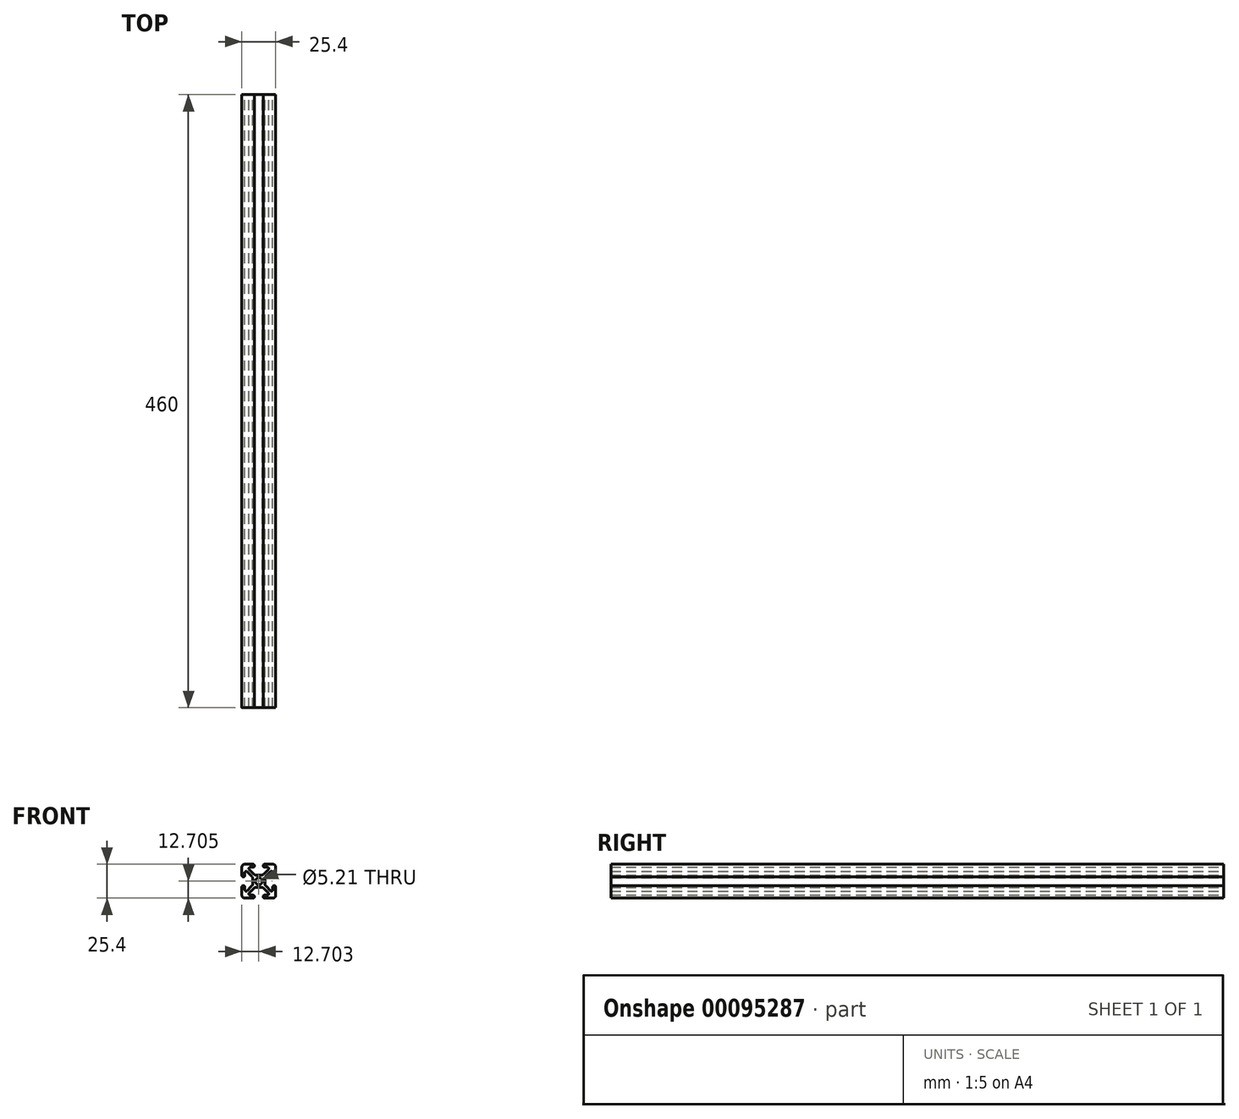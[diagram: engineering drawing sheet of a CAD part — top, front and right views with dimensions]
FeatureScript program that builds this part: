
annotation { "Feature Type Name" : "Feature", "Feature Type Description" : "" }
export const myFeature = defineFeature(function(context is Context, id is Id, definition is map)
    precondition{}
    {
        {
            var Q0;
            Q0=qCreatedBy(makeId("Front.planeOp"),FACE);
            var sketch = newSketch(context, id + "F0", { "sketchPlane" : qUnion([Q0])});
            skArc(sketch, "E0", {"start": v(-10.62, 12.76) * mm, "mid": v(-12.1, 12.15) * mm, "end": v(-12.73, 10.66) * mm});
            skArc(sketch, "E1", {"start": v(-12.73, 4.4) * mm, "mid": v(-11.62, 3.3) * mm, "end": v(-10.52, 4.4) * mm});
            skArc(sketch, "E2", {"start": v(-4.37, 10.55) * mm, "mid": v(-3.27, 11.66) * mm, "end": v(-4.37, 12.76) * mm});
            skArc(sketch, "E3", {"start": v(-8.75, 7.2) * mm, "mid": v(-9.88, 7.42) * mm, "end": v(-10.52, 6.46) * mm});
            skArc(sketch, "E4", {"start": v(-6.43, 10.55) * mm, "mid": v(-7.38, 9.92) * mm, "end": v(-7.16, 8.8) * mm});
            skLineSegment(sketch, "E5", {"start": v(-12.73, 10.66) * mm, "end": v(-12.73, 4.4) * mm});
            skLineSegment(sketch, "E6", {"start": v(-10.62, 12.76) * mm, "end": v(-4.37, 12.76) * mm});
            skLineSegment(sketch, "E7", {"start": v(-10.52, 4.4) * mm, "end": v(-10.52, 6.46) * mm});
            skLineSegment(sketch, "E8", {"start": v(-4.37, 10.55) * mm, "end": v(-6.43, 10.55) * mm});
            skLineSegment(sketch, "E9", {"start": v(-11.51, 7.5) * mm, "end": v(-10.3, 7.5) * mm, "construction": true});
            skLineSegment(sketch, "E10", {"start": v(-13.64, 3.3) * mm, "end": v(-12.36, 3.3) * mm, "construction": true});
            skLineSegment(sketch, "E11", {"start": v(-7.46, 11.03) * mm, "end": v(-7.46, 8.91) * mm, "construction": true});
            skLineSegment(sketch, "E12", {"start": v(-3.27, 12.37) * mm, "end": v(-3.27, 10.25) * mm, "construction": true});
            skLineSegment(sketch, "E13.bottom", {"start": v(1.57, 4.57) * mm, "end": v(-1.63, 4.57) * mm});
            skLineSegment(sketch, "E13.top", {"start": v(1.57, -4.44) * mm, "end": v(-1.63, -4.44) * mm});
            skLineSegment(sketch, "E13.left", {"start": v(4.48, 1.66) * mm, "end": v(4.48, -1.53) * mm});
            skLineSegment(sketch, "E13.right", {"start": v(-4.54, 1.66) * mm, "end": v(-4.54, -1.53) * mm});
            skPoint(sketch, "E13.middle", {"position": v(-0.03, 0.06) * mm});
            skLineSegment(sketch, "E14", {"start": v(-8.75, 7.2) * mm, "end": v(-5.47, 3.9) * mm});
            skLineSegment(sketch, "E15", {"start": v(-7.16, 8.8) * mm, "end": v(-3.87, 5.5) * mm});
            skArc(sketch, "E16.filletArc", {"start": v(-3.87, 5.5) * mm, "mid": v(-2.84, 4.81) * mm, "end": v(-1.63, 4.57) * mm});
            skArc(sketch, "E17.filletArc", {"start": v(-4.54, 1.66) * mm, "mid": v(-4.78, 2.88) * mm, "end": v(-5.47, 3.9) * mm});
            skLineSegment(sketch, "E18", {"start": v(5.32, 0.06) * mm, "end": v(-7.21, 0.06) * mm, "construction": true});
            skPoint(sketch, "E18.startSnap0", {"position": v(2.97, 0.06) * mm});
            skPoint(sketch, "E19", {"position": v(-0.03, -4.44) * mm});
            skLineSegment(sketch, "E20", {"start": v(-0.03, -6.76) * mm, "end": v(-0.03, 5.83) * mm, "construction": true});
            skLineSegment(sketch, "E21.MirrorCS", {"start": v(11.46, 7.5) * mm, "end": v(10.25, 7.5) * mm, "construction": true});
            skArc(sketch, "E22.MirrorCS", {"start": v(10.57, 12.76) * mm, "mid": v(12.06, 12.15) * mm, "end": v(12.67, 10.66) * mm});
            skLineSegment(sketch, "E23.MirrorCS", {"start": v(7.4, 11.03) * mm, "end": v(7.4, 8.91) * mm, "construction": true});
            skLineSegment(sketch, "E24.MirrorCS", {"start": v(10.46, 4.4) * mm, "end": v(10.46, 6.46) * mm});
            skArc(sketch, "E25.MirrorCS", {"start": v(3.82, 5.5) * mm, "mid": v(2.79, 4.81) * mm, "end": v(1.57, 4.57) * mm});
            skLineSegment(sketch, "E26.MirrorCS", {"start": v(8.7, 7.2) * mm, "end": v(5.41, 3.9) * mm});
            skLineSegment(sketch, "E27.MirrorCS", {"start": v(3.21, 12.37) * mm, "end": v(3.21, 10.25) * mm, "construction": true});
            skLineSegment(sketch, "E28.MirrorCS", {"start": v(13.58, 3.3) * mm, "end": v(12.3, 3.3) * mm, "construction": true});
            skArc(sketch, "E29.MirrorCS", {"start": v(4.32, 10.55) * mm, "mid": v(3.21, 11.66) * mm, "end": v(4.32, 12.76) * mm});
            skArc(sketch, "E30.MirrorCS", {"start": v(8.7, 7.2) * mm, "mid": v(9.83, 7.42) * mm, "end": v(10.46, 6.46) * mm});
            skArc(sketch, "E31.MirrorCS", {"start": v(12.67, 4.4) * mm, "mid": v(11.57, 3.3) * mm, "end": v(10.46, 4.4) * mm});
            skLineSegment(sketch, "E32.MirrorCS", {"start": v(10.57, 12.76) * mm, "end": v(4.32, 12.76) * mm});
            skLineSegment(sketch, "E33.MirrorCS", {"start": v(12.67, 10.66) * mm, "end": v(12.67, 4.4) * mm});
            skArc(sketch, "E34.MirrorCS", {"start": v(6.37, 10.55) * mm, "mid": v(7.33, 9.92) * mm, "end": v(7.1, 8.8) * mm});
            skLineSegment(sketch, "E35.MirrorCS", {"start": v(7.1, 8.8) * mm, "end": v(3.82, 5.5) * mm});
            skLineSegment(sketch, "E36.MirrorCS", {"start": v(4.32, 10.55) * mm, "end": v(6.37, 10.55) * mm});
            skArc(sketch, "E37.MirrorCS", {"start": v(4.48, 1.66) * mm, "mid": v(4.72, 2.88) * mm, "end": v(5.41, 3.9) * mm});
            skLineSegment(sketch, "E38.MirrorCS", {"start": v(-11.51, -7.37) * mm, "end": v(-10.3, -7.37) * mm, "construction": true});
            skArc(sketch, "E39.MirrorCS", {"start": v(-3.87, -5.37) * mm, "mid": v(-2.84, -4.69) * mm, "end": v(-1.63, -4.44) * mm});
            skArc(sketch, "E40.MirrorCS", {"start": v(-10.62, -12.64) * mm, "mid": v(-12.1, -12.02) * mm, "end": v(-12.73, -10.53) * mm});
            skArc(sketch, "E41.MirrorCS", {"start": v(-8.75, -7.07) * mm, "mid": v(-9.88, -7.3) * mm, "end": v(-10.52, -6.33) * mm});
            skArc(sketch, "E42.MirrorCS", {"start": v(-6.43, -10.43) * mm, "mid": v(-7.38, -9.79) * mm, "end": v(-7.16, -8.66) * mm});
            skLineSegment(sketch, "E43.MirrorCS", {"start": v(-3.27, -12.24) * mm, "end": v(-3.27, -10.12) * mm, "construction": true});
            skArc(sketch, "E44.MirrorCS", {"start": v(-4.54, -1.53) * mm, "mid": v(-4.78, -2.75) * mm, "end": v(-5.47, -3.78) * mm});
            skLineSegment(sketch, "E45.MirrorCS", {"start": v(-12.73, -10.53) * mm, "end": v(-12.73, -4.28) * mm});
            skLineSegment(sketch, "E46.MirrorCS", {"start": v(-13.64, -3.17) * mm, "end": v(-12.36, -3.17) * mm, "construction": true});
            skLineSegment(sketch, "E47.MirrorCS", {"start": v(-7.46, -10.9) * mm, "end": v(-7.46, -8.78) * mm, "construction": true});
            skLineSegment(sketch, "E48.MirrorCS", {"start": v(-4.37, -10.43) * mm, "end": v(-6.43, -10.43) * mm});
            skLineSegment(sketch, "E49.MirrorCS", {"start": v(-10.62, -12.64) * mm, "end": v(-4.37, -12.64) * mm});
            skLineSegment(sketch, "E50.MirrorCS", {"start": v(-10.52, -4.28) * mm, "end": v(-10.52, -6.33) * mm});
            skArc(sketch, "E51.MirrorCS", {"start": v(-12.73, -4.28) * mm, "mid": v(-11.62, -3.17) * mm, "end": v(-10.52, -4.28) * mm});
            skLineSegment(sketch, "E52.MirrorCS", {"start": v(-8.75, -7.07) * mm, "end": v(-5.47, -3.78) * mm});
            skLineSegment(sketch, "E53.MirrorCS", {"start": v(-7.16, -8.66) * mm, "end": v(-3.87, -5.37) * mm});
            skArc(sketch, "E54.MirrorCS", {"start": v(-4.37, -10.43) * mm, "mid": v(-3.27, -11.53) * mm, "end": v(-4.37, -12.64) * mm});
            skLineSegment(sketch, "E55.MirrorCS", {"start": v(11.46, -7.37) * mm, "end": v(10.25, -7.37) * mm, "construction": true});
            skArc(sketch, "E56.MirrorCS", {"start": v(4.32, -10.43) * mm, "mid": v(3.21, -11.53) * mm, "end": v(4.32, -12.64) * mm});
            skLineSegment(sketch, "E57.MirrorCS", {"start": v(13.58, -3.17) * mm, "end": v(12.3, -3.17) * mm, "construction": true});
            skArc(sketch, "E58.MirrorCS", {"start": v(8.7, -7.07) * mm, "mid": v(9.83, -7.3) * mm, "end": v(10.46, -6.33) * mm});
            skLineSegment(sketch, "E59.MirrorCS", {"start": v(7.1, -8.66) * mm, "end": v(3.82, -5.37) * mm});
            skLineSegment(sketch, "E60.MirrorCS", {"start": v(7.4, -10.9) * mm, "end": v(7.4, -8.78) * mm, "construction": true});
            skLineSegment(sketch, "E61.MirrorCS", {"start": v(3.21, -12.24) * mm, "end": v(3.21, -10.12) * mm, "construction": true});
            skLineSegment(sketch, "E62.MirrorCS", {"start": v(4.32, -10.43) * mm, "end": v(6.37, -10.43) * mm});
            skArc(sketch, "E63.MirrorCS", {"start": v(3.82, -5.37) * mm, "mid": v(2.79, -4.69) * mm, "end": v(1.57, -4.44) * mm});
            skArc(sketch, "E64.MirrorCS", {"start": v(10.57, -12.64) * mm, "mid": v(12.06, -12.02) * mm, "end": v(12.67, -10.53) * mm});
            skLineSegment(sketch, "E65.MirrorCS", {"start": v(10.57, -12.64) * mm, "end": v(4.32, -12.64) * mm});
            skLineSegment(sketch, "E66.MirrorCS", {"start": v(8.7, -7.07) * mm, "end": v(5.41, -3.78) * mm});
            skLineSegment(sketch, "E67.MirrorCS", {"start": v(12.67, -10.53) * mm, "end": v(12.67, -4.28) * mm});
            skArc(sketch, "E68.MirrorCS", {"start": v(12.67, -4.28) * mm, "mid": v(11.57, -3.17) * mm, "end": v(10.46, -4.28) * mm});
            skArc(sketch, "E69.MirrorCS", {"start": v(4.48, -1.53) * mm, "mid": v(4.72, -2.75) * mm, "end": v(5.41, -3.78) * mm});
            skLineSegment(sketch, "E70.MirrorCS", {"start": v(10.46, -4.28) * mm, "end": v(10.46, -6.33) * mm});
            skArc(sketch, "E71.MirrorCS", {"start": v(6.37, -10.43) * mm, "mid": v(7.33, -9.79) * mm, "end": v(7.1, -8.66) * mm});
            skCircle(sketch, "E72", {"center": v(-0.03, 0.06) * mm, "radius": 2.6 * mm});
            skSolve(sketch);
        }
        {
            var Q0;
            Q0 = qSketchRegion(id + "F0", true);
            extrude(context, id + "F1", {"entities" : qUnion([Q0]), "depth" : 460 * mm});
        }
    });
